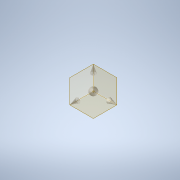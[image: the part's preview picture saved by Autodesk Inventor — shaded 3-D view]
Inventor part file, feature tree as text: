
AUTODESK INVENTOR PART (.ipt)
format: ipt  version: 2022 (Build 260153000, 153)  size: 11,538,432 bytes
history: native  units: mm
features: sketch x8, surface_op x6, plane x3, mirror x2, boolean_combine x2, other x2, loft x1, sweep x1, extrude x1, split x1
ambient origin geometry x8: Origin, YZ Plane, XZ Plane, XY Plane, X Axis, Y Axis, Z Axis, Center Point
bodies: Solid10 (feature_tree), Solid12 (feature_tree), Solid13 (feature_tree)
feature tree (27):
  sketch  "Sketch1"  dims[d3=30.0mm d27=20.0mm]
  sketch  "Sketch2"  dims[d33=7.5mm d34=2.0mm]
  plane  "Work Plane1"
  sketch  "3D Sketch1"
  sketch  "Sketch4"  dims[d35=0.0mm d36=90.0deg d37=0.0mm d38=90.0deg]
  plane  "Work Plane2"
  sketch  "Sketch6"  dims[d39=-7.5mm]
  loft  "Loft1"
  plane  "Work Plane3"
  sweep  "Sweep13"
  mirror  "Mirror3"
  mirror  "Mirror4"
  sketch  "Sketch8"  dims[d43=7.5mm d44=310.0mm d45=0.0mm d46=0.0mm d47=680.0mm d48=90.0deg d49=50.0mm d51=70.0mm d52=0.0mm d53=0.0mm d62=70.0mm d63=2184.75mm d64=3451.75mm d65=47138.5mm d66=69536.75mm d50=0.5mm d54=0.872665mm]
  boolean_combine  "Combine1"
  extrude  "Extrusion2"  TaperAngle=0.0deg  [1 undecoded]
  boolean_combine  "Combine2"
  surface_op  "Extend4"
  surface_op  "Extend5"
  surface_op  "Extend6"
  surface_op  "Extend7"
  surface_op  "Extend8"
  split  "Split1"
  sketch  "Sketch7"  dims[d42=20.0mm]
  other  "Pattern of Solid10:2"
  sketch  "3D Sketch2"
  other  "Srf1"
  surface_op  "Boundary Patch1"
note: 1 required parameter value undecoded (feature->parameter linkage not recoverable at this tier; creation-order binding heuristic only, values carry confidence <= 0.55)
